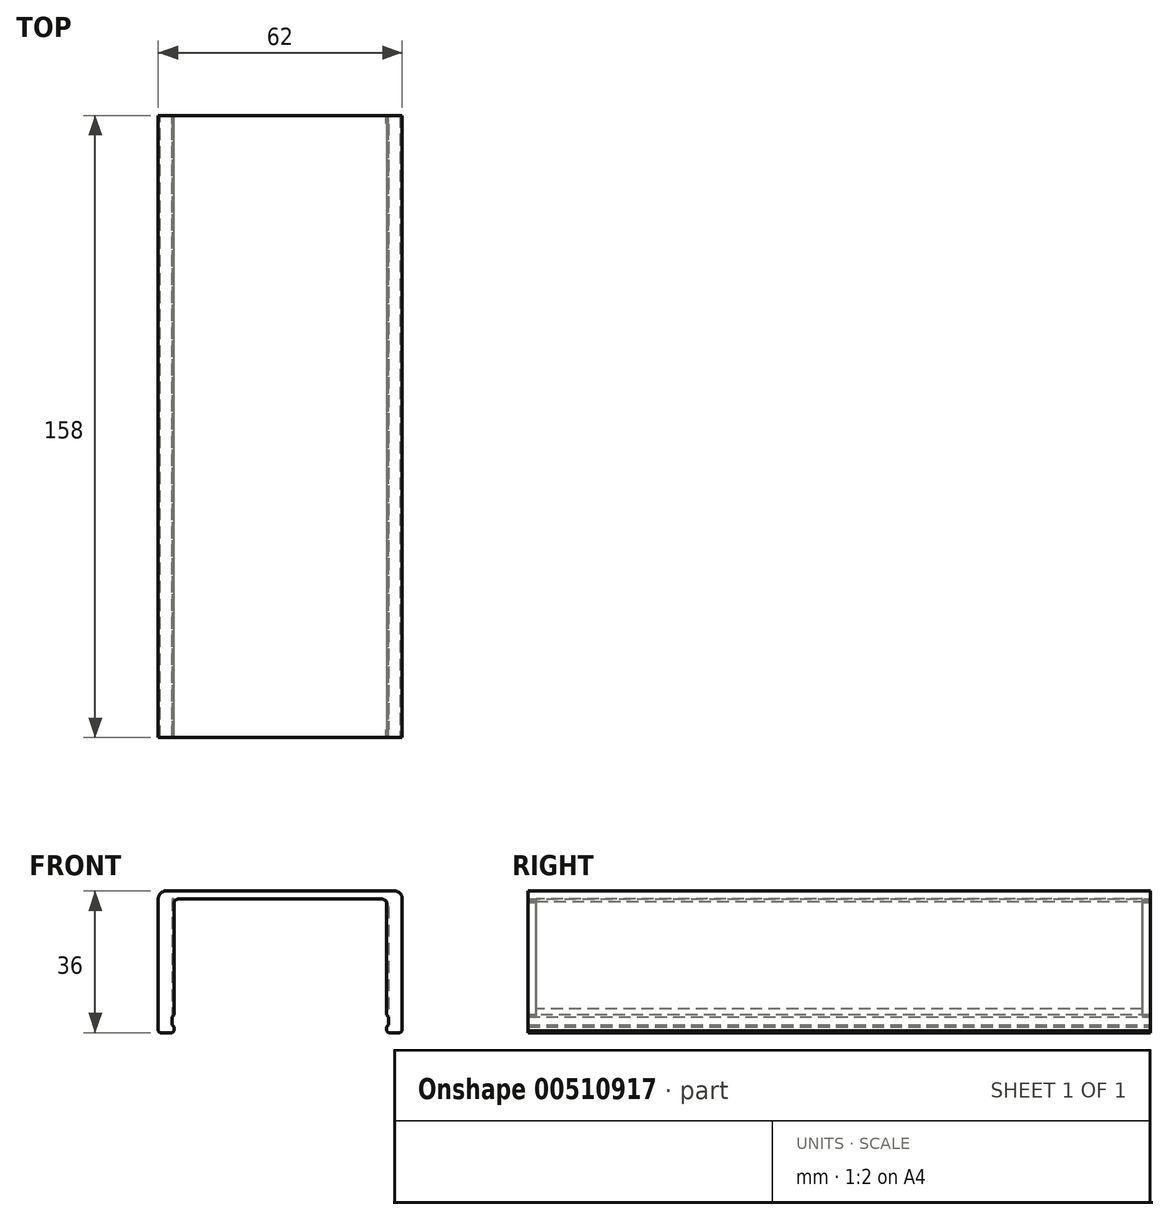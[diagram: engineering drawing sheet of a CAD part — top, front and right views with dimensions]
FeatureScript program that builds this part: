
annotation { "Feature Type Name" : "Feature", "Feature Type Description" : "" }
export const myFeature = defineFeature(function(context is Context, id is Id, definition is map)
    precondition{}
    {
        {
            assignVariable(context, id + "F0", {"name" : "WallThickness", "anyValue" : 2});
        }
        {
            assignVariable(context, id + "F1", {"name" : "InternalLength", "anyValue" : 150});
        }
        {
            var Q0;
            Q0=qCreatedBy(makeId("Front.planeOp"),FACE);
            var sketch = newSketch(context, id + "F2", { "sketchPlane" : qUnion([Q0])});
            skLineSegment(sketch, "E0", {"start": v(-27, -17) * mm, "end": v(-27.5, -17) * mm});
            skLineSegment(sketch, "E1", {"start": v(-27.5, -17) * mm, "end": v(-27.5, -15) * mm});
            skLineSegment(sketch, "E2", {"start": v(-27.5, -15) * mm, "end": v(-27, -15) * mm});
            skLineSegment(sketch, "E3", {"start": v(-27, -15) * mm, "end": v(-27, 15) * mm});
            skLineSegment(sketch, "E4", {"start": v(-27, 15) * mm, "end": v(0, 15) * mm});
            skLineSegment(sketch, "E5", {"start": v(-27, -17) * mm, "end": v(-27, -19) * mm});
            skLineSegment(sketch, "E6", {"start": v(-27, -19) * mm, "end": v(-31, -19) * mm});
            skLineSegment(sketch, "E7", {"start": v(-31, -19) * mm, "end": v(-31, 15) * mm});
            skLineSegment(sketch, "E8", {"start": v(-29, 17) * mm, "end": v(0, 17) * mm});
            skLineSegment(sketch, "E9", {"start": v(-27, 15) * mm, "end": v(-27.5, 15) * mm});
            skLineSegment(sketch, "E10", {"start": v(-27.5, 15) * mm, "end": v(-27.5, -15) * mm});
            skPoint(sketch, "E11", {"position": v(-27, 0) * mm});
            skLineSegment(sketch, "E12", {"start": v(-27, -15) * mm, "end": v(-27, -13) * mm});
            skLineSegment(sketch, "E13", {"start": v(-27, -13) * mm, "end": v(-27.5, -13) * mm});
            skLineSegment(sketch, "E14.MirrorCS", {"start": v(27.5, -15) * mm, "end": v(27, -15) * mm});
            skLineSegment(sketch, "E15.MirrorCS", {"start": v(27, -15) * mm, "end": v(27, -13) * mm});
            skLineSegment(sketch, "E16.MirrorCS", {"start": v(27, 15) * mm, "end": v(27.5, 15) * mm});
            skLineSegment(sketch, "E17.MirrorCS", {"start": v(27, -17) * mm, "end": v(27, -19) * mm});
            skLineSegment(sketch, "E18.MirrorCS", {"start": v(27, -17) * mm, "end": v(27.5, -17) * mm});
            skLineSegment(sketch, "E19.MirrorCS", {"start": v(27.5, -17) * mm, "end": v(27.5, -15) * mm});
            skLineSegment(sketch, "E20.MirrorCS", {"start": v(27, -13) * mm, "end": v(27.5, -13) * mm});
            skLineSegment(sketch, "E21.MirrorCS", {"start": v(27.5, 15) * mm, "end": v(27.5, -15) * mm});
            skLineSegment(sketch, "E22.MirrorCS", {"start": v(29, 17) * mm, "end": v(0, 17) * mm});
            skLineSegment(sketch, "E23.MirrorCS", {"start": v(31, -19) * mm, "end": v(31, 15) * mm});
            skLineSegment(sketch, "E24.MirrorCS", {"start": v(27, -19) * mm, "end": v(31, -19) * mm});
            skLineSegment(sketch, "E25.MirrorCS", {"start": v(27, -15) * mm, "end": v(27, 15) * mm});
            skLineSegment(sketch, "E26.MirrorCS", {"start": v(27, 15) * mm, "end": v(0, 15) * mm});
            skPoint(sketch, "E27.MirrorP", {"position": v(27, 0) * mm});
            skPoint(sketch, "E28.visualSharp", {"position": v(-31, 17) * mm});
            skArc(sketch, "E28.filletArc", {"start": v(-29, 17) * mm, "mid": v(-30.41, 16.41) * mm, "end": v(-31, 15) * mm});
            skPoint(sketch, "E29.visualSharp", {"position": v(31, 17) * mm});
            skArc(sketch, "E29.filletArc", {"start": v(31, 15) * mm, "mid": v(30.41, 16.41) * mm, "end": v(29, 17) * mm});
            skArc(sketch, "E30", {"start": v(-25.5, 15) * mm, "mid": v(-26.91, 14.41) * mm, "end": v(-27.5, 13) * mm});
            skArc(sketch, "E31", {"start": v(27.5, 13) * mm, "mid": v(26.91, 14.41) * mm, "end": v(25.5, 15) * mm});
            skSolve(sketch);
        }
        {
            var Q0;
            Q0 = qSketchRegion(id + "F2", true);
            extrude(context, id + "F3", {"entities" : qUnion([Q0]), "endBound" : BoundingType.SYMMETRIC, "depth" : (getVariable(context, 'InternalLength') + 4 * getVariable(context, 'WallThickness')) * mm});
        }
        {
            var Q0;
            Q0=makeQuery(id+"F2.imprint","IMPRINT",FACE,{"disambiguationData":[TD([[makeQuery(id+"F2.imprint","IMPRINT",EDGE,{"derivedFrom":sQuery(id+"F2.wireOp",EDGE,"E3")}),1.0]])]});
            var Q1;
            {var subQ0=sQuery(id+"F2.wireOp",EDGE,"E20.MirrorCS");Q1=makeQuery(id+"F2.imprint","IMPRINT",FACE,{"disambiguationData":[TD([[makeQuery(id+"F2.imprint","IMPRINT",EDGE,{"derivedFrom":subQ0}),1.0]])]});}
            extrude(context, id + "F4", {"entities" : qUnion([Q0, Q1]), "operationType" : NewBodyOperationType.REMOVE, "endBound" : BoundingType.SYMMETRIC, "oppositeDirection" : true, "depth" : (getVariable(context, 'InternalLength') + 2 * getVariable(context, 'WallThickness')) * mm});
        }
        {
            var Q0;
            Q0=makeQuery(id+"F3.opExtrude","SWEPT_EDGE",EDGE,{"disambiguationData":[OSD([sQuery(id+"F2.wireOp",EDGE,"E0"),sQuery(id+"F2.wireOp",EDGE,"E5")])]});
            var Q1;
            Q1=makeQuery(id+"F3.opExtrude","SWEPT_EDGE",EDGE,{"disambiguationData":[OSD([sQuery(id+"F2.wireOp",EDGE,"E2"),sQuery(id+"F2.wireOp",EDGE,"E12")])]});
            var Q2;
            Q2=makeQuery(id+"F3.opExtrude","SWEPT_EDGE",EDGE,{"disambiguationData":[OSD([sQuery(id+"F2.wireOp",EDGE,"E14.MirrorCS"),sQuery(id+"F2.wireOp",EDGE,"E25.MirrorCS")])]});
            var Q3;
            Q3=makeQuery(id+"F3.opExtrude","SWEPT_EDGE",EDGE,{"disambiguationData":[OSD([sQuery(id+"F2.wireOp",EDGE,"E17.MirrorCS"),sQuery(id+"F2.wireOp",EDGE,"E18.MirrorCS")])]});
            var Q4;
            Q4=makeQuery(id+"F3.opExtrude","SWEPT_EDGE",EDGE,{"disambiguationData":[OSD([sQuery(id+"F2.wireOp",EDGE,"E5"),sQuery(id+"F2.wireOp",EDGE,"E6")])]});
            var Q5;
            Q5=makeQuery(id+"F3.opExtrude","SWEPT_EDGE",EDGE,{"disambiguationData":[OSD([sQuery(id+"F2.wireOp",EDGE,"E17.MirrorCS"),sQuery(id+"F2.wireOp",EDGE,"E24.MirrorCS")])]});
            var Q6;
            Q6=makeQuery(id+"F3.opExtrude","SWEPT_EDGE",EDGE,{"disambiguationData":[OSD([sQuery(id+"F2.wireOp",EDGE,"E6"),sQuery(id+"F2.wireOp",EDGE,"E7")])]});
            var Q7;
            Q7=makeQuery(id+"F3.opExtrude","SWEPT_EDGE",EDGE,{"disambiguationData":[OSD([sQuery(id+"F2.wireOp",EDGE,"E23.MirrorCS"),sQuery(id+"F2.wireOp",EDGE,"E24.MirrorCS")])]});
            chamfer(context, id + "F5", {"entities" : qUnion([Q0, Q1, Q2, Q3, Q4, Q5, Q6, Q7]), "width" : (getVariable(context, 'WallThickness') / 4) * mm, "tangentPropagation" : true});
        }
    });
